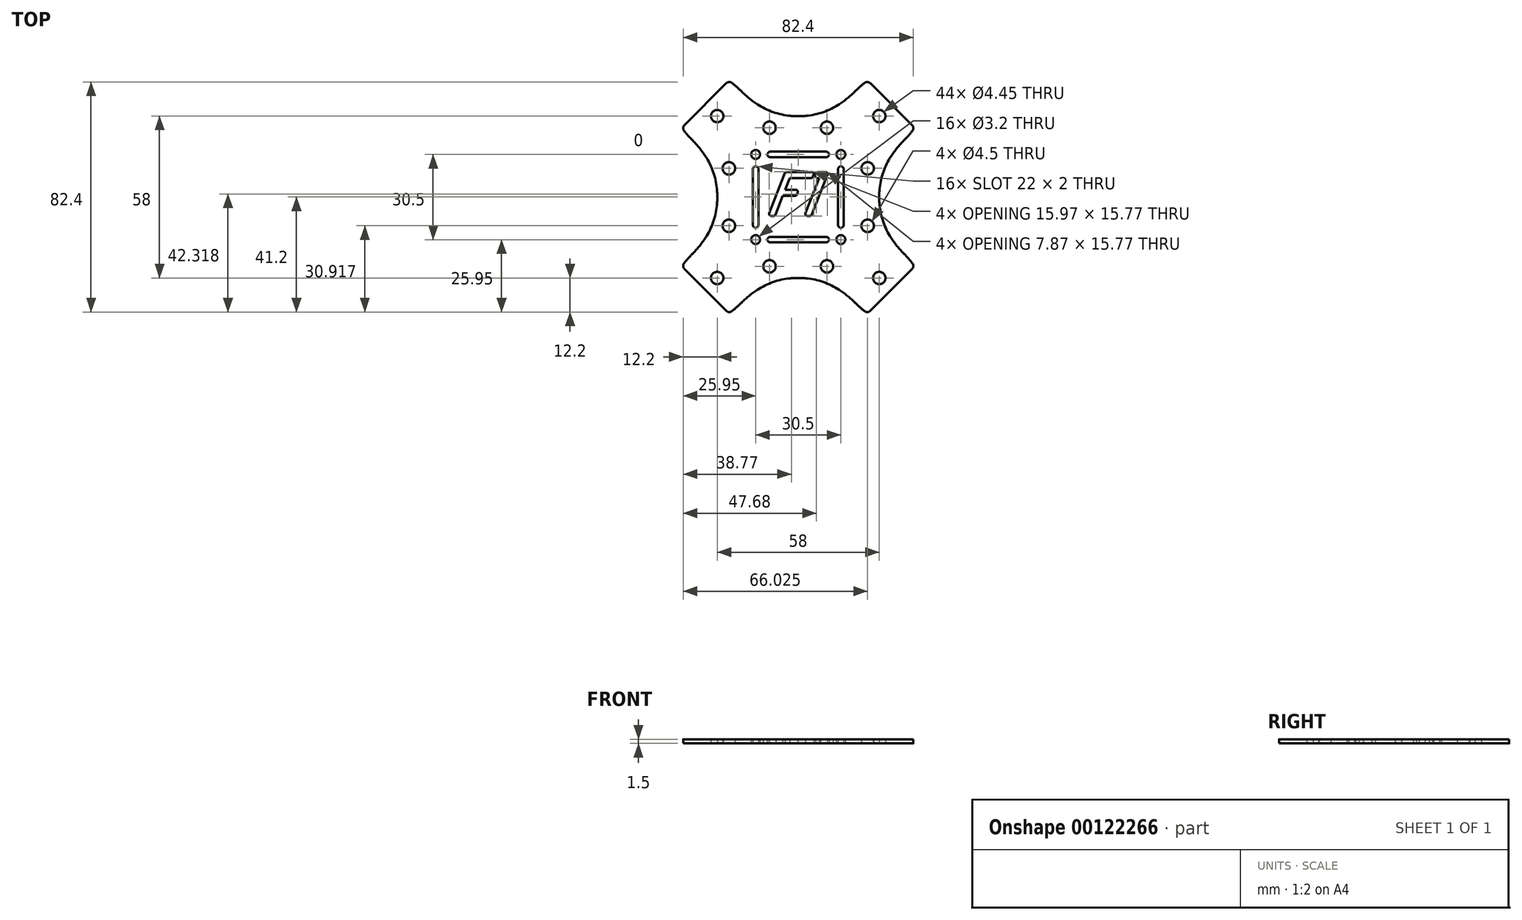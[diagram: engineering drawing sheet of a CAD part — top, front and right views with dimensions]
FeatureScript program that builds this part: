
annotation { "Feature Type Name" : "Feature", "Feature Type Description" : "" }
export const myFeature = defineFeature(function(context is Context, id is Id, definition is map)
    precondition{}
    {
        {
            var Q0;
            Q0=qCreatedBy(makeId("Top.planeOp"),FACE);
            var sketch = newSketch(context, id + "F0", { "sketchPlane" : qUnion([Q0])});
            skArc(sketch, "E0", {"start": v(2.6, -5.75) * mm, "mid": v(2.67, -6.44) * mm, "end": v(3.3, -6.77) * mm});
            skLineSegment(sketch, "E1", {"start": v(4.11, -6.77) * mm, "end": v(3.3, -6.77) * mm});
            skArc(sketch, "E2", {"start": v(4.11, -6.77) * mm, "mid": v(4.53, -6.64) * mm, "end": v(4.8, -6.3) * mm});
            skLineSegment(sketch, "E3", {"start": v(-1.2, 0.4) * mm, "end": v(-5.54, 0.4) * mm});
            skArc(sketch, "E4", {"start": v(-1.2, 0.4) * mm, "mid": v(-0.77, 0.54) * mm, "end": v(-0.5, 0.89) * mm});
            skLineSegment(sketch, "E5", {"start": v(-0.22, 1.6) * mm, "end": v(-0.5, 0.89) * mm});
            skArc(sketch, "E6", {"start": v(-0.22, 1.6) * mm, "mid": v(-0.3, 2.29) * mm, "end": v(-0.92, 2.62) * mm});
            skLineSegment(sketch, "E7", {"start": v(6.25, 7.82) * mm, "end": v(6.53, 8.53) * mm});
            skArc(sketch, "E8", {"start": v(6.25, 7.82) * mm, "mid": v(6.33, 7.12) * mm, "end": v(6.95, 6.8) * mm});
            skLineSegment(sketch, "E9", {"start": v(4.53, 6.8) * mm, "end": v(-3.05, 6.8) * mm});
            skArc(sketch, "E10", {"start": v(4.53, 6.8) * mm, "mid": v(4.96, 6.93) * mm, "end": v(5.23, 7.27) * mm});
            skLineSegment(sketch, "E11", {"start": v(5.5, 7.98) * mm, "end": v(5.23, 7.27) * mm});
            skArc(sketch, "E12", {"start": v(5.5, 7.98) * mm, "mid": v(5.43, 8.68) * mm, "end": v(4.8, 9) * mm});
            skLineSegment(sketch, "E13", {"start": v(10.37, 7.98) * mm, "end": v(4.8, -6.3) * mm});
            skArc(sketch, "E14", {"start": v(10.37, 7.98) * mm, "mid": v(10.29, 8.68) * mm, "end": v(9.67, 9) * mm});
            skLineSegment(sketch, "E15", {"start": v(-4.11, 9) * mm, "end": v(4.8, 9) * mm});
            skArc(sketch, "E16", {"start": v(-4.11, 9) * mm, "mid": v(-4.53, 8.87) * mm, "end": v(-4.8, 8.53) * mm});
            skArc(sketch, "E17", {"start": v(25.75, 40.76) * mm, "mid": v(24.78, 41.2) * mm, "end": v(23.77, 40.89) * mm});
            skArc(sketch, "E18", {"start": v(23.77, 40.89) * mm, "mid": v(21.96, 39.38) * mm, "end": v(20.24, 37.76) * mm});
            skArc(sketch, "E19", {"start": v(14.65, 33.23) * mm, "mid": v(17.56, 35.35) * mm, "end": v(20.24, 37.76) * mm});
            skArc(sketch, "E20", {"start": v(2.83, 29.1) * mm, "mid": v(9, 30.45) * mm, "end": v(14.65, 33.23) * mm});
            skArc(sketch, "E21", {"start": v(-2.83, 29.1) * mm, "mid": v(0, 28.97) * mm, "end": v(2.83, 29.1) * mm});
            skArc(sketch, "E22", {"start": v(-14.65, 33.23) * mm, "mid": v(-9, 30.45) * mm, "end": v(-2.83, 29.1) * mm});
            skArc(sketch, "E23", {"start": v(-20.24, 37.76) * mm, "mid": v(-17.56, 35.35) * mm, "end": v(-14.65, 33.23) * mm});
            skArc(sketch, "E24", {"start": v(-20.24, 37.76) * mm, "mid": v(-21.96, 39.38) * mm, "end": v(-23.77, 40.89) * mm});
            skArc(sketch, "E25", {"start": v(-23.77, 40.89) * mm, "mid": v(-24.78, 41.2) * mm, "end": v(-25.75, 40.76) * mm});
            skLineSegment(sketch, "E26", {"start": v(-25.75, 40.76) * mm, "end": v(-40.76, 25.75) * mm});
            skArc(sketch, "E27", {"start": v(-40.76, 25.75) * mm, "mid": v(-41.2, 24.78) * mm, "end": v(-40.89, 23.77) * mm});
            skArc(sketch, "E28", {"start": v(-40.89, 23.77) * mm, "mid": v(-39.38, 21.96) * mm, "end": v(-37.76, 20.24) * mm});
            skArc(sketch, "E29", {"start": v(-33.23, 14.65) * mm, "mid": v(-35.35, 17.56) * mm, "end": v(-37.76, 20.24) * mm});
            skArc(sketch, "E30", {"start": v(-29.1, 2.83) * mm, "mid": v(-30.45, 9) * mm, "end": v(-33.23, 14.65) * mm});
            skArc(sketch, "E31", {"start": v(-29.1, -2.83) * mm, "mid": v(-28.97, 0) * mm, "end": v(-29.1, 2.83) * mm});
            skArc(sketch, "E32", {"start": v(-33.23, -14.65) * mm, "mid": v(-30.45, -9) * mm, "end": v(-29.1, -2.83) * mm});
            skArc(sketch, "E33", {"start": v(-37.76, -20.24) * mm, "mid": v(-35.35, -17.56) * mm, "end": v(-33.23, -14.65) * mm});
            skArc(sketch, "E34", {"start": v(-37.76, -20.24) * mm, "mid": v(-39.38, -21.96) * mm, "end": v(-40.89, -23.77) * mm});
            skArc(sketch, "E35", {"start": v(-40.89, -23.77) * mm, "mid": v(-41.2, -24.78) * mm, "end": v(-40.76, -25.75) * mm});
            skLineSegment(sketch, "E36", {"start": v(-40.76, -25.75) * mm, "end": v(-25.75, -40.76) * mm});
            skArc(sketch, "E37", {"start": v(-25.75, -40.76) * mm, "mid": v(-24.78, -41.2) * mm, "end": v(-23.77, -40.89) * mm});
            skArc(sketch, "E38", {"start": v(-23.77, -40.89) * mm, "mid": v(-21.96, -39.38) * mm, "end": v(-20.24, -37.76) * mm});
            skArc(sketch, "E39", {"start": v(-14.65, -33.23) * mm, "mid": v(-17.56, -35.35) * mm, "end": v(-20.24, -37.76) * mm});
            skArc(sketch, "E40", {"start": v(-2.83, -29.1) * mm, "mid": v(-9, -30.45) * mm, "end": v(-14.65, -33.23) * mm});
            skArc(sketch, "E41", {"start": v(2.83, -29.1) * mm, "mid": v(0, -28.97) * mm, "end": v(-2.83, -29.1) * mm});
            skArc(sketch, "E42", {"start": v(14.65, -33.23) * mm, "mid": v(9, -30.45) * mm, "end": v(2.83, -29.1) * mm});
            skArc(sketch, "E43", {"start": v(20.24, -37.76) * mm, "mid": v(17.56, -35.35) * mm, "end": v(14.65, -33.23) * mm});
            skArc(sketch, "E44", {"start": v(20.24, -37.76) * mm, "mid": v(21.96, -39.38) * mm, "end": v(23.77, -40.89) * mm});
            skArc(sketch, "E45", {"start": v(23.77, -40.89) * mm, "mid": v(24.78, -41.2) * mm, "end": v(25.75, -40.76) * mm});
            skLineSegment(sketch, "E46", {"start": v(25.75, -40.76) * mm, "end": v(40.76, -25.75) * mm});
            skArc(sketch, "E47", {"start": v(40.76, -25.75) * mm, "mid": v(41.2, -24.78) * mm, "end": v(40.89, -23.77) * mm});
            skArc(sketch, "E48", {"start": v(40.89, -23.77) * mm, "mid": v(39.38, -21.96) * mm, "end": v(37.76, -20.24) * mm});
            skArc(sketch, "E49", {"start": v(33.23, -14.65) * mm, "mid": v(35.35, -17.56) * mm, "end": v(37.76, -20.24) * mm});
            skArc(sketch, "E50", {"start": v(29.1, -2.83) * mm, "mid": v(30.45, -9) * mm, "end": v(33.23, -14.65) * mm});
            skArc(sketch, "E51", {"start": v(29.1, 2.83) * mm, "mid": v(28.97, 0) * mm, "end": v(29.1, -2.83) * mm});
            skArc(sketch, "E52", {"start": v(33.23, 14.65) * mm, "mid": v(30.45, 9) * mm, "end": v(29.1, 2.83) * mm});
            skArc(sketch, "E53", {"start": v(37.76, 20.24) * mm, "mid": v(35.35, 17.56) * mm, "end": v(33.23, 14.65) * mm});
            skArc(sketch, "E54", {"start": v(37.76, 20.24) * mm, "mid": v(39.38, 21.96) * mm, "end": v(40.89, 23.77) * mm});
            skArc(sketch, "E55", {"start": v(40.89, 23.77) * mm, "mid": v(41.2, 24.78) * mm, "end": v(40.76, 25.75) * mm});
            skLineSegment(sketch, "E56", {"start": v(40.76, 25.75) * mm, "end": v(25.75, 40.76) * mm});
            skCircle(sketch, "E57", {"center": v(-15.25, 15.25) * mm, "radius": 1.6 * mm});
            skCircle(sketch, "E58", {"center": v(-29, 29) * mm, "radius": 2.23 * mm});
            skCircle(sketch, "E59", {"center": v(-10.28, 24.82) * mm, "radius": 2.23 * mm});
            skCircle(sketch, "E60", {"center": v(-24.82, 10.28) * mm, "radius": 2.23 * mm});
            skCircle(sketch, "E61", {"center": v(-15.25, -15.25) * mm, "radius": 1.6 * mm});
            skCircle(sketch, "E62", {"center": v(-29, -29) * mm, "radius": 2.23 * mm});
            skCircle(sketch, "E63", {"center": v(-10.28, -24.82) * mm, "radius": 2.23 * mm});
            skCircle(sketch, "E64", {"center": v(-24.82, -10.28) * mm, "radius": 2.23 * mm});
            skCircle(sketch, "E65", {"center": v(15.25, -15.25) * mm, "radius": 1.6 * mm});
            skCircle(sketch, "E66", {"center": v(29, -29) * mm, "radius": 2.23 * mm});
            skCircle(sketch, "E67", {"center": v(10.28, -24.82) * mm, "radius": 2.23 * mm});
            skCircle(sketch, "E68", {"center": v(24.82, -10.28) * mm, "radius": 2.25 * mm});
            skCircle(sketch, "E69", {"center": v(15.25, 15.25) * mm, "radius": 1.6 * mm});
            skCircle(sketch, "E70", {"center": v(29, 29) * mm, "radius": 2.23 * mm});
            skCircle(sketch, "E71", {"center": v(10.28, 24.82) * mm, "radius": 2.23 * mm});
            skCircle(sketch, "E72", {"center": v(24.82, 10.28) * mm, "radius": 2.23 * mm});
            skLineSegment(sketch, "E73", {"start": v(7.48, 6.8) * mm, "end": v(6.95, 6.8) * mm});
            skLineSegment(sketch, "E74", {"start": v(-5.54, 0.4) * mm, "end": v(-8.15, -6.3) * mm});
            skLineSegment(sketch, "E75", {"start": v(-4.68, 2.62) * mm, "end": v(-0.92, 2.62) * mm});
            skLineSegment(sketch, "E76", {"start": v(-3.05, 6.8) * mm, "end": v(-4.68, 2.62) * mm});
            skLineSegment(sketch, "E77", {"start": v(10, 14.25) * mm, "end": v(-10, 14.25) * mm});
            skArc(sketch, "E78", {"start": v(10, 14.25) * mm, "mid": v(11, 15.25) * mm, "end": v(10, 16.25) * mm});
            skLineSegment(sketch, "E79", {"start": v(-10, 16.25) * mm, "end": v(10, 16.25) * mm});
            skArc(sketch, "E80", {"start": v(-10, 16.25) * mm, "mid": v(-11, 15.25) * mm, "end": v(-10, 14.25) * mm});
            skLineSegment(sketch, "E81", {"start": v(10, -14.25) * mm, "end": v(-10, -14.25) * mm});
            skArc(sketch, "E82", {"start": v(10, -16.25) * mm, "mid": v(11, -15.25) * mm, "end": v(10, -14.25) * mm});
            skLineSegment(sketch, "E83", {"start": v(-10, -16.25) * mm, "end": v(10, -16.25) * mm});
            skArc(sketch, "E84", {"start": v(-10, -14.25) * mm, "mid": v(-11, -15.25) * mm, "end": v(-10, -16.25) * mm});
            skLineSegment(sketch, "E85", {"start": v(-14.25, 10) * mm, "end": v(-14.25, -10) * mm});
            skArc(sketch, "E86", {"start": v(-14.25, 10) * mm, "mid": v(-15.25, 11) * mm, "end": v(-16.25, 10) * mm});
            skLineSegment(sketch, "E87", {"start": v(-16.25, -10) * mm, "end": v(-16.25, 10) * mm});
            skArc(sketch, "E88", {"start": v(-16.25, -10) * mm, "mid": v(-15.25, -11) * mm, "end": v(-14.25, -10) * mm});
            skLineSegment(sketch, "E89", {"start": v(14.25, 10) * mm, "end": v(14.25, -10) * mm});
            skArc(sketch, "E90", {"start": v(16.25, 10) * mm, "mid": v(15.25, 11) * mm, "end": v(14.25, 10) * mm});
            skLineSegment(sketch, "E91", {"start": v(16.25, -10) * mm, "end": v(16.25, 10) * mm});
            skArc(sketch, "E92", {"start": v(14.25, -10) * mm, "mid": v(15.25, -11) * mm, "end": v(16.25, -10) * mm});
            skLineSegment(sketch, "E93", {"start": v(7.23, 9) * mm, "end": v(9.67, 9) * mm});
            skArc(sketch, "E94", {"start": v(7.23, 9) * mm, "mid": v(6.8, 8.87) * mm, "end": v(6.53, 8.53) * mm});
            skLineSegment(sketch, "E95", {"start": v(-8.85, -6.77) * mm, "end": v(-9.67, -6.77) * mm});
            skArc(sketch, "E96", {"start": v(-8.85, -6.77) * mm, "mid": v(-8.43, -6.64) * mm, "end": v(-8.15, -6.3) * mm});
            skLineSegment(sketch, "E97", {"start": v(-10.37, -5.75) * mm, "end": v(-4.8, 8.53) * mm});
            skArc(sketch, "E98", {"start": v(-10.37, -5.75) * mm, "mid": v(-10.29, -6.44) * mm, "end": v(-9.67, -6.77) * mm});
            skLineSegment(sketch, "E99", {"start": v(2.6, -5.75) * mm, "end": v(7.48, 6.8) * mm});
            skSolve(sketch);
        }
        {
            var Q0;
            Q0 = qSketchRegion(id + "F0", true);
            extrude(context, id + "F1", {"entities" : qUnion([Q0]), "depth" : 1.5 * mm});
        }
    });
